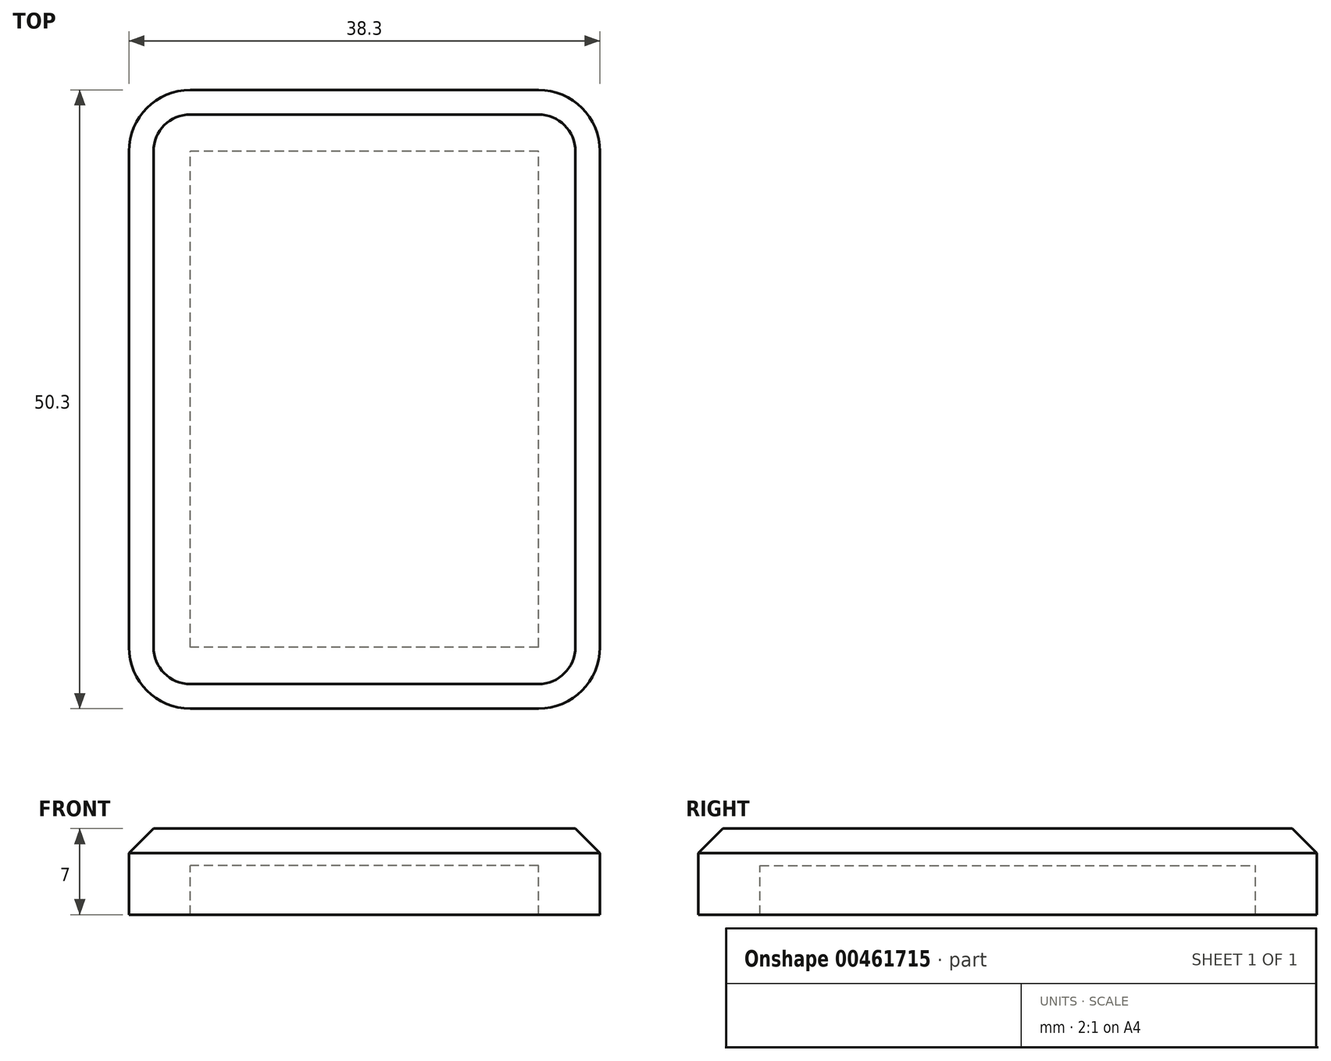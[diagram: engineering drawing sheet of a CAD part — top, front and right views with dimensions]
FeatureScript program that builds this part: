
annotation { "Feature Type Name" : "Feature", "Feature Type Description" : "" }
export const myFeature = defineFeature(function(context is Context, id is Id, definition is map)
    precondition{}
    {
        {
            var Q0;
            Q0=qCreatedBy(makeId("Top.planeOp"),FACE);
            var sketch = newSketch(context, id + "F0", { "sketchPlane" : qUnion([Q0])});
            skLineSegment(sketch, "E0.bottom", {"start": v(14.15, -20.15) * mm, "end": v(-14.15, -20.15) * mm});
            skLineSegment(sketch, "E0.top", {"start": v(14.15, 20.15) * mm, "end": v(-14.15, 20.15) * mm});
            skLineSegment(sketch, "E0.left", {"start": v(14.15, -20.15) * mm, "end": v(14.15, 20.15) * mm});
            skLineSegment(sketch, "E0.right", {"start": v(-14.15, -20.15) * mm, "end": v(-14.15, 20.15) * mm});
            skPoint(sketch, "E0.middle", {"position": v(0, 0) * mm});
            skLineSegment(sketch, "E1.0", {"start": v(19.15, 25.15) * mm, "end": v(-19.15, 25.15) * mm});
            skLineSegment(sketch, "E1.1", {"start": v(19.15, -25.15) * mm, "end": v(19.15, 25.15) * mm});
            skLineSegment(sketch, "E1.2", {"start": v(19.15, -25.15) * mm, "end": v(-19.15, -25.15) * mm});
            skLineSegment(sketch, "E1.3", {"start": v(-19.15, -25.15) * mm, "end": v(-19.15, 25.15) * mm});
            skSolve(sketch);
        }
        {
            var Q0;
            Q0=qCreatedBy(makeId("Top.planeOp"),FACE);
            cPlane(context, id + "F1", {"entities" : qUnion([Q0]), "cplaneType" : CPlaneType.OFFSET, "offset" : 10 * mm, "width" : 150 * mm, "height" : 150 * mm});
        }
        {
            var Q0;
            Q0=makeQuery(id+"F0.imprint","IMPRINT",FACE,{"disambiguationData":[TD([[makeQuery(id+"F0.imprint","IMPRINT",EDGE,{"derivedFrom":sQuery(id+"F0.wireOp",EDGE,"E0.bottom")}),1.0]])]});
            extrude(context, id + "F2", {"entities" : qUnion([Q0]), "oppositeDirection" : true, "depth" : 4 * mm});
        }
        {
            var Q0;
            Q0=qSketchRegion(id+"F0",true);
            var Q1;
            Q1=makeQuery(id+"F0.imprint","IMPRINT",FACE,{"disambiguationData":[TD([[makeQuery(id+"F0.imprint","IMPRINT",EDGE,{"derivedFrom":sQuery(id+"F0.wireOp",EDGE,"E0.bottom")}),-1.0]])]});
            extrude(context, id + "F3", {"entities" : qUnion([Q0, Q1]), "operationType" : NewBodyOperationType.ADD, "depth" : 3 * mm});
        }
        {
            var Q0;
            {var subQ0=sQuery(id+"F0.wireOp",EDGE,"E1.3");var subQ1=sQuery(id+"F0.wireOp",EDGE,"E1.2");Q0=makeQuery(id+"F3.boolean.opBoolean","MERGE",EDGE,{"derivedFrom":[makeQuery(id+"F2.opExtrude","SWEPT_EDGE",EDGE,{"disambiguationData":[OSD([subQ1,subQ0])]}),makeQuery(id+"F3.opExtrude","SWEPT_EDGE",EDGE,{"disambiguationData":[OSD([subQ1,subQ0])]})]});}
            var Q1;
            {var subQ0=sQuery(id+"F0.wireOp",EDGE,"E1.3");var subQ1=sQuery(id+"F0.wireOp",EDGE,"E1.0");Q1=makeQuery(id+"F3.boolean.opBoolean","MERGE",EDGE,{"derivedFrom":[makeQuery(id+"F2.opExtrude","SWEPT_EDGE",EDGE,{"disambiguationData":[OSD([subQ1,subQ0])]}),makeQuery(id+"F3.opExtrude","SWEPT_EDGE",EDGE,{"disambiguationData":[OSD([subQ1,subQ0])]})]});}
            var Q2;
            {var subQ0=sQuery(id+"F0.wireOp",EDGE,"E1.1");var subQ1=sQuery(id+"F0.wireOp",EDGE,"E1.0");Q2=makeQuery(id+"F3.boolean.opBoolean","MERGE",EDGE,{"derivedFrom":[makeQuery(id+"F2.opExtrude","SWEPT_EDGE",EDGE,{"disambiguationData":[OSD([subQ1,subQ0])]}),makeQuery(id+"F3.opExtrude","SWEPT_EDGE",EDGE,{"disambiguationData":[OSD([subQ1,subQ0])]})]});}
            var Q3;
            {var subQ0=sQuery(id+"F0.wireOp",EDGE,"E1.2");var subQ1=sQuery(id+"F0.wireOp",EDGE,"E1.1");Q3=makeQuery(id+"F3.boolean.opBoolean","MERGE",EDGE,{"derivedFrom":[makeQuery(id+"F2.opExtrude","SWEPT_EDGE",EDGE,{"disambiguationData":[OSD([subQ1,subQ0])]}),makeQuery(id+"F3.opExtrude","SWEPT_EDGE",EDGE,{"disambiguationData":[OSD([subQ1,subQ0])]})]});}
            fillet(context, id + "F4", {"entities" : qUnion([Q0, Q1, Q2, Q3]), "radius" : 5 * mm, "tangentPropagation" : true, "allowEdgeOverflow" : false});
        }
        {
            var Q0;
            Q0=makeQuery(id+"F3.opExtrude","CAP_FACE",FACE,{"disambiguationData":[OSD([sQuery(id+"F0.wireOp",EDGE,"E1.0"),sQuery(id+"F0.wireOp",EDGE,"E1.1"),sQuery(id+"F0.wireOp",EDGE,"E1.2"),sQuery(id+"F0.wireOp",EDGE,"E1.3")])],"isStart":false});
            chamfer(context, id + "F5", {"entities" : qUnion([Q0]), "width" : 2 * mm, "tangentPropagation" : true});
        }
    });
